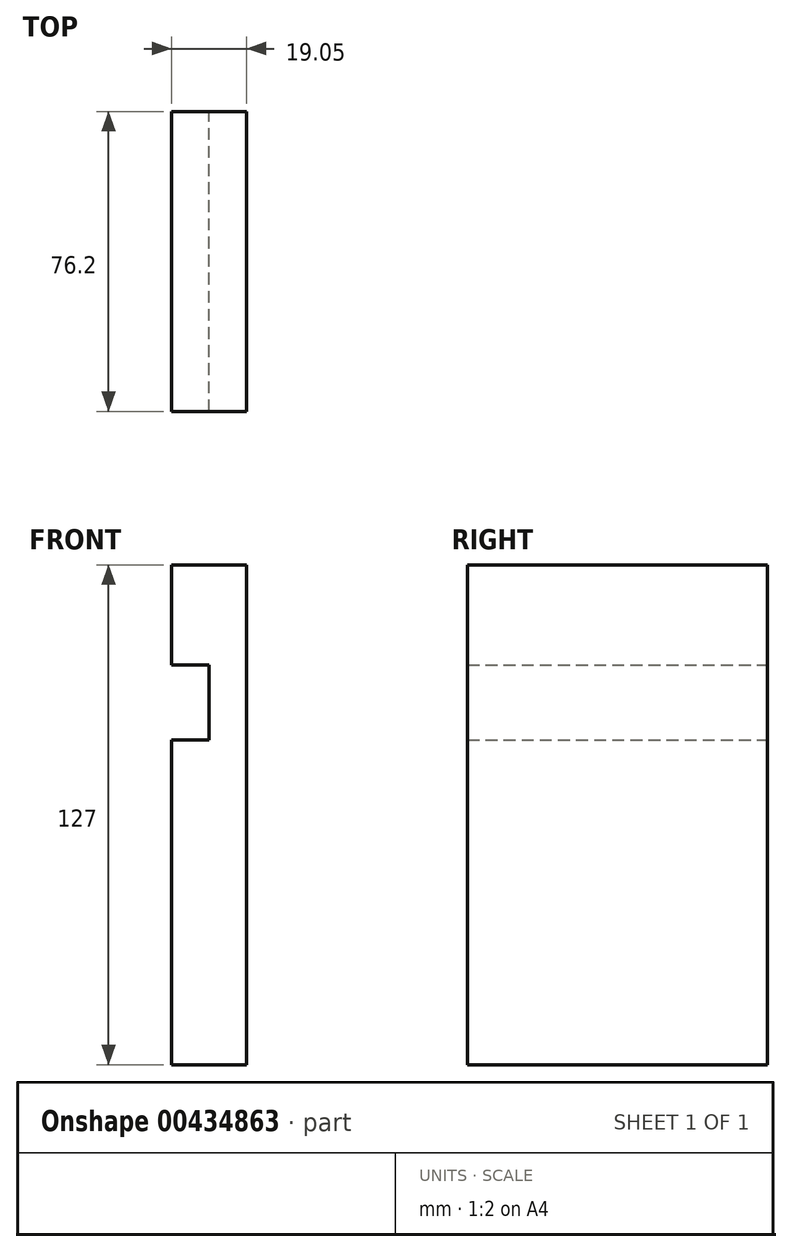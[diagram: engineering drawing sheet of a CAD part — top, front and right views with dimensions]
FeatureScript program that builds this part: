
annotation { "Feature Type Name" : "Feature", "Feature Type Description" : "" }
export const myFeature = defineFeature(function(context is Context, id is Id, definition is map)
    precondition{}
    {
        {
            var Q0;
            Q0=qCreatedBy(makeId("Front.planeOp"),FACE);
            var sketch = newSketch(context, id + "F0", { "sketchPlane" : qUnion([Q0])});
            skLineSegment(sketch, "E0", {"start": v(9.12, 86.14) * mm, "end": v(9.12, -40.86) * mm});
            skLineSegment(sketch, "E1", {"start": v(9.12, -40.86) * mm, "end": v(-9.93, -40.86) * mm});
            skLineSegment(sketch, "E2", {"start": v(-9.93, -40.86) * mm, "end": v(-9.93, 41.69) * mm});
            skLineSegment(sketch, "E3", {"start": v(-9.93, 41.69) * mm, "end": v(-0.4, 41.69) * mm});
            skLineSegment(sketch, "E4", {"start": v(-0.4, 41.69) * mm, "end": v(-0.4, 60.74) * mm});
            skLineSegment(sketch, "E5", {"start": v(-0.4, 60.74) * mm, "end": v(-9.93, 60.74) * mm});
            skLineSegment(sketch, "E6", {"start": v(-9.93, 60.74) * mm, "end": v(-9.93, 86.14) * mm});
            skLineSegment(sketch, "E7", {"start": v(-9.93, 86.14) * mm, "end": v(9.12, 86.14) * mm});
            skSolve(sketch);
        }
        {
            var Q0;
            Q0=makeQuery(id+"F0.imprint","IMPRINT",FACE,{"disambiguationData":[TD([[makeQuery(id+"F0.imprint","IMPRINT",EDGE,{"derivedFrom":sQuery(id+"F0.wireOp",EDGE,"E0")}),-1.0]])]});
            extrude(context, id + "F1", {"entities" : qUnion([Q0]), "depth" : 76.2 * mm});
        }
    });
